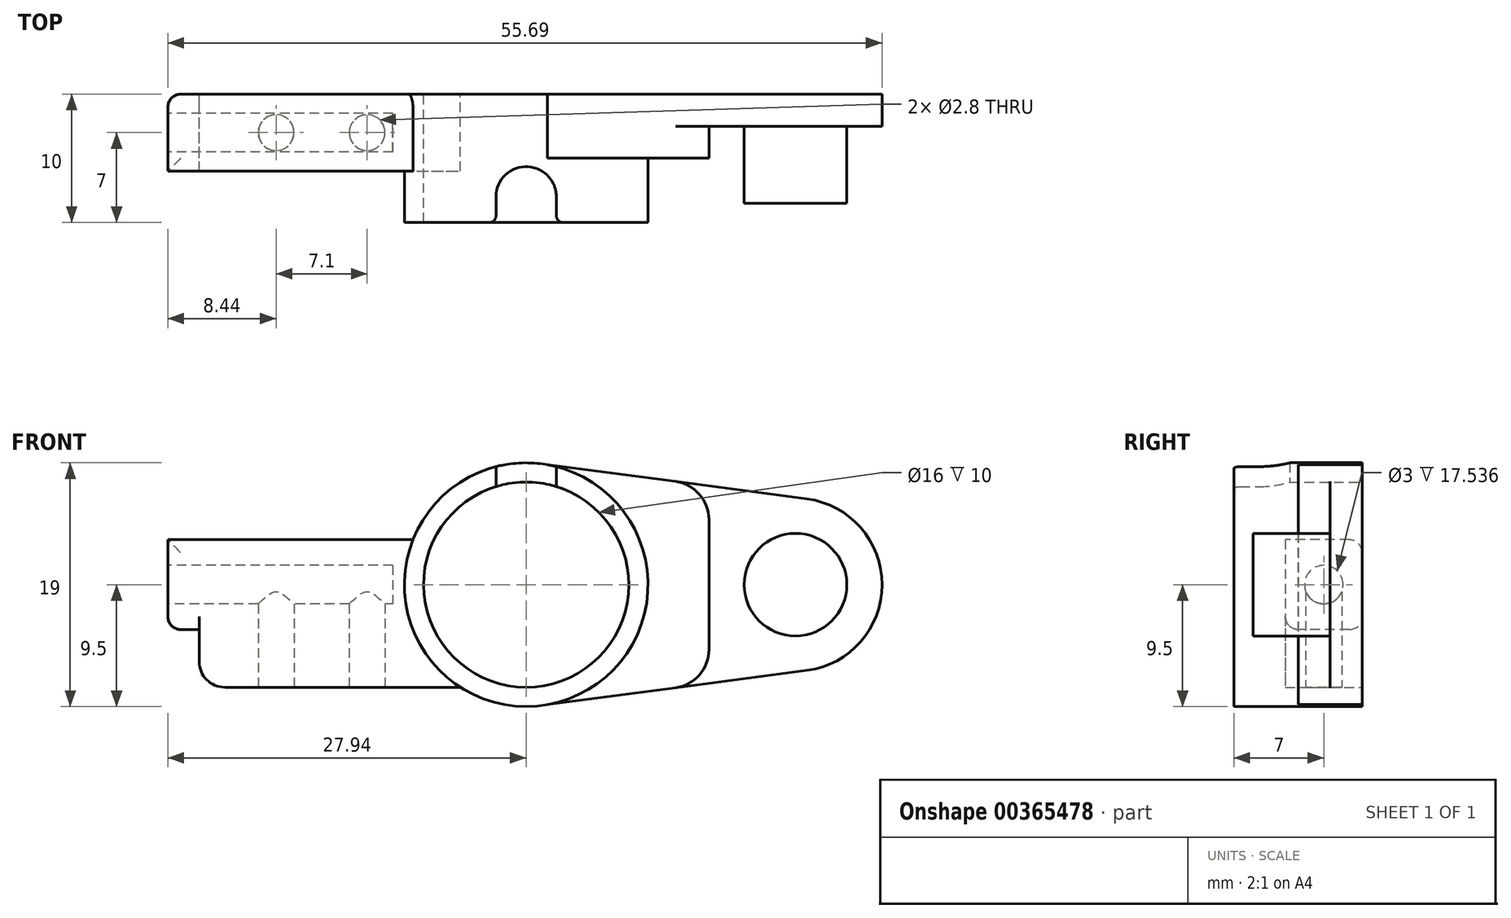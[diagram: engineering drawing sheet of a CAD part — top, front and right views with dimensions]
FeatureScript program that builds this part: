
annotation { "Feature Type Name" : "Feature", "Feature Type Description" : "" }
export const myFeature = defineFeature(function(context is Context, id is Id, definition is map)
    precondition{}
    {
        {
            var Q0;
            Q0=qCreatedBy(makeId("Front.planeOp"),FACE);
            var sketch = newSketch(context, id + "F0", { "sketchPlane" : qUnion([Q0])});
            skCircle(sketch, "E0", {"center": v(0, 0) * mm, "radius": 8 * mm});
            skCircle(sketch, "E1", {"center": v(0, 0) * mm, "radius": 9.5 * mm});
            skLineSegment(sketch, "E2", {"start": v(0, 0) * mm, "end": v(0, -1.5) * mm});
            skLineSegment(sketch, "E3", {"start": v(0, 0) * mm, "end": v(0, 1.5) * mm});
            skLineSegment(sketch, "E4", {"start": v(-32.5, 0) * mm, "end": v(-32.5, 1.5) * mm});
            skLineSegment(sketch, "E5", {"start": v(-32.5, 0) * mm, "end": v(-32.5, -1.5) * mm});
            skLineSegment(sketch, "E6", {"start": v(-32.5, -1.5) * mm, "end": v(-32.5, -2.5) * mm});
            skLineSegment(sketch, "E7", {"start": v(-23.5, -8) * mm, "end": v(-5.12, -8) * mm});
            skLineSegment(sketch, "E8.MirrorCS", {"start": v(-32.5, 1.5) * mm, "end": v(-32.5, 3.5) * mm});
            skLineSegment(sketch, "E9", {"start": v(-25.5, 0) * mm, "end": v(-25.5, -6) * mm});
            skLineSegment(sketch, "E10", {"start": v(-32.5, 1.5) * mm, "end": v(-32.5, 2.5) * mm});
            skLineSegment(sketch, "E11", {"start": v(-32.5, -1.5) * mm, "end": v(-32.5, -3.5) * mm});
            skLineSegment(sketch, "E12", {"start": v(-31.5, -3.5) * mm, "end": v(-25.5, -3.5) * mm});
            skLineSegment(sketch, "E13", {"start": v(-31.5, 3.5) * mm, "end": v(-25.5, 3.5) * mm});
            skPoint(sketch, "E14.orphan", {"position": v(-32.5, 8) * mm});
            skPoint(sketch, "E15.orphan", {"position": v(-32.5, -8) * mm});
            skPoint(sketch, "E16.visualSharp", {"position": v(-25.5, 8) * mm});
            skPoint(sketch, "E17.visualSharp", {"position": v(-25.5, -8) * mm});
            skArc(sketch, "E17.filletArc", {"start": v(-25.5, -6) * mm, "mid": v(-24.91, -7.41) * mm, "end": v(-23.5, -8) * mm});
            skPoint(sketch, "E18.visualSharp", {"position": v(-32.5, 3.5) * mm});
            skArc(sketch, "E18.filletArc", {"start": v(-31.5, 3.5) * mm, "mid": v(-32.2, 3.2) * mm, "end": v(-32.5, 2.5) * mm});
            skPoint(sketch, "E19.visualSharp", {"position": v(-32.5, -3.5) * mm});
            skArc(sketch, "E19.filletArc", {"start": v(-32.5, -2.5) * mm, "mid": v(-32.2, -3.2) * mm, "end": v(-31.5, -3.5) * mm});
            skPoint(sketch, "E20.orphan", {"position": v(-2.5, 8) * mm});
            skPoint(sketch, "E21.orphan", {"position": v(-2.5, -8) * mm});
            skLineSegment(sketch, "E22", {"start": v(-25.5, 3.5) * mm, "end": v(-8.83, 3.5) * mm});
            skLineSegment(sketch, "E23", {"start": v(-25.5, -3.5) * mm, "end": v(-25.5, 3) * mm});
            skLineSegment(sketch, "E24", {"start": v(-23.5, 5) * mm, "end": v(-8.08, 5) * mm});
            skPoint(sketch, "E25.visualSharp", {"position": v(-25.5, 5) * mm});
            skArc(sketch, "E25.filletArc", {"start": v(-23.5, 5) * mm, "mid": v(-24.91, 4.41) * mm, "end": v(-25.5, 3) * mm});
            skSolve(sketch);
        }
        {
            var Q0;
            Q0=qSketchRegion(id+"F0",true);
            extrude(context, id + "F1", {"entities" : qUnion([Q0]), "depth" : 10 * mm});
        }
        {
            var Q0;
            Q0=makeQuery(id+"F1.opExtrude","SWEPT_FACE",FACE,{"disambiguationData":[OSD([sQuery(id+"F0.wireOp",EDGE,"E7")])]});
            var sketch = newSketch(context, id + "F2", { "sketchPlane" : qUnion([Q0])});
            skLineSegment(sketch, "E26", {"start": v(-11, 3) * mm, "end": v(-12.4, 3) * mm});
            skCircle(sketch, "E27", {"center": v(-12.4, 3) * mm, "radius": 1.4 * mm});
            skLineSegment(sketch, "E28", {"start": v(-23.5, 5) * mm, "end": v(-22.5, 5) * mm});
            skCircle(sketch, "E29", {"center": v(-19.5, 3) * mm, "radius": 1.4 * mm});
            skSolve(sketch);
        }
        {
            var Q0;
            Q0=qSketchRegion(id+"F2",true);
            extrude(context, id + "F3", {"entities" : qUnion([Q0]), "operationType" : NewBodyOperationType.REMOVE, "oppositeDirection" : true, "depth" : 8 * mm});
        }
        {
            var Q0;
            Q0=qCreatedBy(makeId("Front.planeOp"),FACE);
            var sketch = newSketch(context, id + "F4", { "sketchPlane" : qUnion([Q0])});
            skLineSegment(sketch, "E30", {"start": v(8.71, 0) * mm, "end": v(21, 0) * mm});
            skCircle(sketch, "E31", {"center": v(21, 0) * mm, "radius": 6.75 * mm});
            skLineSegment(sketch, "E32", {"start": v(21, 0) * mm, "end": v(21, -5.45) * mm});
            skLineSegment(sketch, "E33", {"start": v(21, 0) * mm, "end": v(21.88, -6.7) * mm});
            skLineSegment(sketch, "E34", {"start": v(21.88, -6.7) * mm, "end": v(0.83, -9.46) * mm});
            skArc(sketch, "E35", {"start": v(0.83, -9.46) * mm, "mid": v(1.24, -9.42) * mm, "end": v(1.65, -9.36) * mm});
            skArc(sketch, "E36.MirrorCS", {"start": v(0.83, 9.46) * mm, "mid": v(1.24, 9.42) * mm, "end": v(1.65, 9.36) * mm});
            skLineSegment(sketch, "E37.MirrorCS", {"start": v(21.88, 6.7) * mm, "end": v(0.83, 9.46) * mm});
            skArc(sketch, "E38", {"start": v(0.83, -8.67) * mm, "mid": v(8.71, 0) * mm, "end": v(0.83, 8.67) * mm});
            skLineSegment(sketch, "E39", {"start": v(0.83, 9.46) * mm, "end": v(0.83, 8.67) * mm});
            skPoint(sketch, "E40.orphan", {"position": v(9.5, 0) * mm});
            skLineSegment(sketch, "E41.trimOffspring", {"start": v(0.83, -8.67) * mm, "end": v(0.83, -9.46) * mm});
            skSolve(sketch);
        }
        {
            var Q0;
            Q0=qSketchRegion(id+"F4",true);
            extrude(context, id + "F5", {"entities" : qUnion([Q0]), "operationType" : NewBodyOperationType.ADD, "depth" : 2.5 * mm});
        }
        {
            var Q0;
            Q0=makeQuery(id+"F5.opExtrude","CAP_FACE",FACE,{"disambiguationData":[OSD([sQuery(id+"F4.wireOp",EDGE,"E31"),sQuery(id+"F4.wireOp",EDGE,"E34"),sQuery(id+"F4.wireOp",EDGE,"E35"),sQuery(id+"F4.wireOp",EDGE,"E36.MirrorCS"),sQuery(id+"F4.wireOp",EDGE,"E37.MirrorCS"),sQuery(id+"F4.wireOp",EDGE,"E38"),sQuery(id+"F4.wireOp",EDGE,"E39"),sQuery(id+"F4.wireOp",EDGE,"E41.trimOffspring")])],"isStart":false});
            var sketch = newSketch(context, id + "F6", { "sketchPlane" : qUnion([Q0])});
            skCircle(sketch, "E42", {"center": v(21, 0) * mm, "radius": 4 * mm});
            skSolve(sketch);
        }
        {
            var Q0;
            Q0=qSketchRegion(id+"F6",true);
            extrude(context, id + "F7", {"entities" : qUnion([Q0]), "operationType" : NewBodyOperationType.ADD, "depth" : 6 * mm});
        }
        {
            var Q0;
            Q0=makeQuery(id+"F5.opExtrude","CAP_FACE",FACE,{"disambiguationData":[OSD([sQuery(id+"F4.wireOp",EDGE,"E31"),sQuery(id+"F4.wireOp",EDGE,"E34"),sQuery(id+"F4.wireOp",EDGE,"E35"),sQuery(id+"F4.wireOp",EDGE,"E36.MirrorCS"),sQuery(id+"F4.wireOp",EDGE,"E37.MirrorCS"),sQuery(id+"F4.wireOp",EDGE,"E38"),sQuery(id+"F4.wireOp",EDGE,"E39"),sQuery(id+"F4.wireOp",EDGE,"E41.trimOffspring")])],"isStart":false});
            var sketch = newSketch(context, id + "F8", { "sketchPlane" : qUnion([Q0])});
            skLineSegment(sketch, "E43", {"start": v(14.25, 0) * mm, "end": v(14.25, 7.7) * mm});
            skLineSegment(sketch, "E44", {"start": v(1.65, 9.36) * mm, "end": v(14.25, 7.7) * mm});
            skArc(sketch, "E45", {"start": v(1.65, -8.34) * mm, "mid": v(8.5, 0) * mm, "end": v(1.65, 8.34) * mm});
            skLineSegment(sketch, "E46", {"start": v(1.65, 9.36) * mm, "end": v(1.65, 8.34) * mm});
            skLineSegment(sketch, "E47.MirrorCS", {"start": v(1.65, -9.36) * mm, "end": v(1.65, -8.34) * mm});
            skLineSegment(sketch, "E48.MirrorCS", {"start": v(1.65, -9.36) * mm, "end": v(14.25, -7.7) * mm});
            skLineSegment(sketch, "E49.MirrorCS", {"start": v(14.25, 0) * mm, "end": v(14.25, -7.7) * mm});
            skPoint(sketch, "E50.start.orphan", {"position": v(9.5, 0) * mm});
            skSolve(sketch);
        }
        {
            var Q0;
            Q0=qSketchRegion(id+"F8",true);
            extrude(context, id + "F9", {"entities" : qUnion([Q0]), "operationType" : NewBodyOperationType.ADD, "depth" : 2.5 * mm});
        }
        {
            var Q0;
            Q0=makeQuery(id+"F9.opExtrude","SWEPT_EDGE",EDGE,{"disambiguationData":[OSD([sQuery(id+"F4.wireOp",EDGE,"E37.MirrorCS"),sQuery(id+"F8.wireOp",EDGE,"E43"),sQuery(id+"F8.wireOp",EDGE,"E44")])]});
            var Q1;
            Q1=makeQuery(id+"F9.opExtrude","SWEPT_EDGE",EDGE,{"disambiguationData":[OSD([sQuery(id+"F4.wireOp",EDGE,"E34"),sQuery(id+"F8.wireOp",EDGE,"E48.MirrorCS"),sQuery(id+"F8.wireOp",EDGE,"E49.MirrorCS")])]});
            fillet(context, id + "F10", {"entities" : qUnion([Q0, Q1]), "radius" : 3 * mm, "tangentPropagation" : true, "allowEdgeOverflow" : false});
        }
        {
            var Q0;
            Q0=qCreatedBy(makeId("Top.planeOp"),FACE);
            var sketch = newSketch(context, id + "F11", { "sketchPlane" : qUnion([Q0])});
            skLineSegment(sketch, "E51", {"start": v(0, 0) * mm, "end": v(0, -8) * mm});
            skCircle(sketch, "E52", {"center": v(0, -8) * mm, "radius": 2.35 * mm});
            skLineSegment(sketch, "E53.bottom", {"start": v(-2.35, -8) * mm, "end": v(2.35, -8) * mm});
            skLineSegment(sketch, "E53.top", {"start": v(-2.35, -11.86) * mm, "end": v(2.35, -11.86) * mm});
            skLineSegment(sketch, "E53.left", {"start": v(-2.35, -8) * mm, "end": v(-2.35, -11.86) * mm});
            skLineSegment(sketch, "E53.right", {"start": v(2.35, -8) * mm, "end": v(2.35, -11.86) * mm});
            skSolve(sketch);
        }
        {
            var Q0;
            Q0=qSketchRegion(id+"F11",true);
            extrude(context, id + "F12", {"entities" : qUnion([Q0]), "operationType" : NewBodyOperationType.REMOVE, "depth" : 25 * mm});
        }
        {
            var Q0;
            Q0=makeQuery(id+"F12.boolean.opBoolean","INTERSECT",EDGE,{"derivedFrom":[makeQuery(id+"F1.opExtrude","CAP_FACE",FACE,{"disambiguationData":[OSD([sQuery(id+"F0.wireOp",EDGE,"E0"),sQuery(id+"F0.wireOp",EDGE,"E1"),sQuery(id+"F0.wireOp",EDGE,"E4"),sQuery(id+"F0.wireOp",EDGE,"E5"),sQuery(id+"F0.wireOp",EDGE,"E7"),sQuery(id+"F0.wireOp",EDGE,"E9"),sQuery(id+"F0.wireOp",EDGE,"E10"),sQuery(id+"F0.wireOp",EDGE,"E11"),sQuery(id+"F0.wireOp",EDGE,"E12"),sQuery(id+"F0.wireOp",EDGE,"E13"),sQuery(id+"F0.wireOp",EDGE,"E17.filletArc"),sQuery(id+"F0.wireOp",EDGE,"E18.filletArc"),sQuery(id+"F0.wireOp",EDGE,"E19.filletArc"),sQuery(id+"F0.wireOp",EDGE,"E22"),sQuery(id+"F0.wireOp",EDGE,"E24"),sQuery(id+"F0.wireOp",EDGE,"E25.filletArc")])],"isStart":false}),makeQuery(id+"F12.opExtrude","SWEPT_FACE",FACE,{"disambiguationData":[OSD([sQuery(id+"F11.wireOp",EDGE,"E53.left")])]})]});
            var Q1;
            Q1=makeQuery(id+"F12.boolean.opBoolean","INTERSECT",EDGE,{"derivedFrom":[makeQuery(id+"F1.opExtrude","CAP_FACE",FACE,{"disambiguationData":[OSD([sQuery(id+"F0.wireOp",EDGE,"E0"),sQuery(id+"F0.wireOp",EDGE,"E1"),sQuery(id+"F0.wireOp",EDGE,"E4"),sQuery(id+"F0.wireOp",EDGE,"E5"),sQuery(id+"F0.wireOp",EDGE,"E7"),sQuery(id+"F0.wireOp",EDGE,"E9"),sQuery(id+"F0.wireOp",EDGE,"E10"),sQuery(id+"F0.wireOp",EDGE,"E11"),sQuery(id+"F0.wireOp",EDGE,"E12"),sQuery(id+"F0.wireOp",EDGE,"E13"),sQuery(id+"F0.wireOp",EDGE,"E17.filletArc"),sQuery(id+"F0.wireOp",EDGE,"E18.filletArc"),sQuery(id+"F0.wireOp",EDGE,"E19.filletArc"),sQuery(id+"F0.wireOp",EDGE,"E22"),sQuery(id+"F0.wireOp",EDGE,"E24"),sQuery(id+"F0.wireOp",EDGE,"E25.filletArc")])],"isStart":false}),makeQuery(id+"F12.opExtrude","SWEPT_FACE",FACE,{"disambiguationData":[OSD([sQuery(id+"F11.wireOp",EDGE,"E53.right")])]})]});
            fillet(context, id + "F13", {"entities" : qUnion([Q0, Q1]), "radius" : 0.5 * mm, "tangentPropagation" : true, "allowEdgeOverflow" : false});
        }
        {
            var Q0;
            Q0=makeQuery(id+"F1.opExtrude","CAP_FACE",FACE,{"disambiguationData":[OSD([sQuery(id+"F0.wireOp",EDGE,"E0"),sQuery(id+"F0.wireOp",EDGE,"E1"),sQuery(id+"F0.wireOp",EDGE,"E4"),sQuery(id+"F0.wireOp",EDGE,"E5"),sQuery(id+"F0.wireOp",EDGE,"E7"),sQuery(id+"F0.wireOp",EDGE,"E9"),sQuery(id+"F0.wireOp",EDGE,"E10"),sQuery(id+"F0.wireOp",EDGE,"E11"),sQuery(id+"F0.wireOp",EDGE,"E12"),sQuery(id+"F0.wireOp",EDGE,"E13"),sQuery(id+"F0.wireOp",EDGE,"E17.filletArc"),sQuery(id+"F0.wireOp",EDGE,"E18.filletArc"),sQuery(id+"F0.wireOp",EDGE,"E19.filletArc"),sQuery(id+"F0.wireOp",EDGE,"E22"),sQuery(id+"F0.wireOp",EDGE,"E24"),sQuery(id+"F0.wireOp",EDGE,"E25.filletArc")])],"isStart":false});
            var sketch = newSketch(context, id + "F14", { "sketchPlane" : qUnion([Q0])});
            skSolve(sketch);
        }
        {
            var Q0;
            Q0=makeQuery(id+"F1.opExtrude","SWEPT_FACE",FACE,{"disambiguationData":[OSD([sQuery(id+"F0.wireOp",EDGE,"E4"),sQuery(id+"F0.wireOp",EDGE,"E5"),sQuery(id+"F0.wireOp",EDGE,"E10"),sQuery(id+"F0.wireOp",EDGE,"E11")])]});
            var sketch = newSketch(context, id + "F15", { "sketchPlane" : qUnion([Q0])});
            skLineSegment(sketch, "E54", {"start": v(0, 0) * mm, "end": v(3, 0) * mm});
            skCircle(sketch, "E55", {"center": v(3, 0) * mm, "radius": 1.5 * mm});
            skLineSegment(sketch, "E56", {"start": v(3, 0) * mm, "end": v(6, 0) * mm});
            skSolve(sketch);
        }
        {
            var Q0;
            Q0 = qSketchRegion(id + "F15", true);
            extrude(context, id + "F16", {"entities" : qUnion([Q0]), "operationType" : NewBodyOperationType.REMOVE, "oppositeDirection" : true, "depth" : 22.1 * mm});
        }
        {
            var Q0;
            {var subQ11=sQuery(id+"F0.wireOp",EDGE,"E7");Q0=makeQuery(id+"F14.imprint","IMPRINT",FACE,{"disambiguationData":[TD([[makeQuery(id+"F14.imprint","IMPRINT",EDGE,{"derivedFrom":makeQuery(id+"F1.opExtrude","CAP_EDGE",EDGE,{"disambiguationData":[OSD([subQ11])],"isStart":false})}),1.0]])]});}
            var sketch = newSketch(context, id + "F17", { "sketchPlane" : qUnion([Q0])});
            skArc(sketch, "E57", {"start": v(-6.07, 7.3) * mm, "mid": v(-9.46, -0.82) * mm, "end": v(-4.73, -8.24) * mm});
            skLineSegment(sketch, "E58.bottom", {"start": v(-34.83, 7.3) * mm, "end": v(-6.07, 7.3) * mm});
            skLineSegment(sketch, "E58.top", {"start": v(-34.83, -9.59) * mm, "end": v(-4.73, -9.59) * mm});
            skLineSegment(sketch, "E58.left", {"start": v(-34.83, 7.3) * mm, "end": v(-34.83, -9.59) * mm});
            skLineSegment(sketch, "E58.right", {"start": v(-4.73, -8.24) * mm, "end": v(-4.73, -9.59) * mm});
            skSolve(sketch);
        }
        {
            var Q0;
            Q0 = qSketchRegion(id + "F17", true);
            extrude(context, id + "F18", {"entities" : qUnion([Q0]), "operationType" : NewBodyOperationType.REMOVE, "oppositeDirection" : true, "depth" : 4 * mm});
        }
        {
            var Q0;
            Q0=makeQuery(id+"F18.boolean.opBoolean","COPY",FACE,{"derivedFrom":makeQuery(id+"F18.opExtrude","CAP_FACE",FACE,{"disambiguationData":[OSD([sQuery(id+"F17.wireOp",EDGE,"E57"),sQuery(id+"F17.wireOp",EDGE,"E58.bottom"),sQuery(id+"F17.wireOp",EDGE,"E58.top"),sQuery(id+"F17.wireOp",EDGE,"E58.left"),sQuery(id+"F17.wireOp",EDGE,"E58.right")])],"isStart":false})});
            var sketch = newSketch(context, id + "F19", { "sketchPlane" : qUnion([Q0])});
            skArc(sketch, "E59", {"start": v(-7.5, 5.84) * mm, "mid": v(-8.25, 4.72) * mm, "end": v(-8.83, 3.5) * mm});
            skLineSegment(sketch, "E60.bottom", {"start": v(-25.44, 3.5) * mm, "end": v(-8.83, 3.5) * mm});
            skLineSegment(sketch, "E60.top", {"start": v(-25.44, 6.51) * mm, "end": v(-7.5, 6.51) * mm});
            skLineSegment(sketch, "E60.right", {"start": v(-7.5, 5.84) * mm, "end": v(-7.5, 6.51) * mm});
            skLineSegment(sketch, "E61", {"start": v(-25.44, 3.5) * mm, "end": v(-27.94, 3.5) * mm});
            skLineSegment(sketch, "E62", {"start": v(-27.94, 3.5) * mm, "end": v(-27.94, -7.75) * mm});
            skLineSegment(sketch, "E63", {"start": v(-27.94, -7.75) * mm, "end": v(-39, -7.75) * mm});
            skLineSegment(sketch, "E64", {"start": v(-39, -7.75) * mm, "end": v(-39, 6.51) * mm});
            skLineSegment(sketch, "E65", {"start": v(-39, 6.51) * mm, "end": v(-25.44, 6.51) * mm});
            skSolve(sketch);
        }
        {
            var Q0;
            Q0 = qSketchRegion(id + "F19", true);
            extrude(context, id + "F20", {"entities" : qUnion([Q0]), "operationType" : NewBodyOperationType.REMOVE, "oppositeDirection" : true, "depth" : 25 * mm});
        }
        {
            var Q0;
            Q0=makeQuery(id+"F20.boolean.opBoolean","COPY",EDGE,{"derivedFrom":makeQuery(id+"F20.opExtrude","SWEPT_EDGE",EDGE,{"disambiguationData":[OSD([sQuery(id+"F0.wireOp",EDGE,"E13"),sQuery(id+"F0.wireOp",EDGE,"E22"),sQuery(id+"F17.wireOp",EDGE,"E57"),sQuery(id+"F17.wireOp",EDGE,"E58.bottom"),sQuery(id+"F17.wireOp",EDGE,"E58.top"),sQuery(id+"F17.wireOp",EDGE,"E58.left"),sQuery(id+"F17.wireOp",EDGE,"E58.right"),sQuery(id+"F19.wireOp",EDGE,"E61"),sQuery(id+"F19.wireOp",EDGE,"E62")])]})});
            var Q1;
            Q1=makeQuery(id+"F20.boolean.opBoolean","INTERSECT",EDGE,{"derivedFrom":[makeQuery(id+"F1.opExtrude","SWEPT_FACE",FACE,{"disambiguationData":[OSD([sQuery(id+"F0.wireOp",EDGE,"E12")])]}),makeQuery(id+"F20.opExtrude","SWEPT_FACE",FACE,{"disambiguationData":[OSD([sQuery(id+"F19.wireOp",EDGE,"E62")])]})]});
            var Q2;
            Q2=makeQuery(id+"F20.boolean.opBoolean","COPY",EDGE,{"derivedFrom":makeQuery(id+"F20.opExtrude","CAP_EDGE",EDGE,{"disambiguationData":[OSD([sQuery(id+"F19.wireOp",EDGE,"E62")])],"isStart":true})});
            var Q3;
            Q3=makeQuery(id+"F20.boolean.opBoolean","INTERSECT",EDGE,{"derivedFrom":[makeQuery(id+"F5.boolean.opBoolean","MERGE",FACE,{"derivedFrom":[makeQuery(id+"F1.opExtrude","CAP_FACE",FACE,{"disambiguationData":[OSD([sQuery(id+"F0.wireOp",EDGE,"E0"),sQuery(id+"F0.wireOp",EDGE,"E1"),sQuery(id+"F0.wireOp",EDGE,"E4"),sQuery(id+"F0.wireOp",EDGE,"E5"),sQuery(id+"F0.wireOp",EDGE,"E7"),sQuery(id+"F0.wireOp",EDGE,"E9"),sQuery(id+"F0.wireOp",EDGE,"E10"),sQuery(id+"F0.wireOp",EDGE,"E11"),sQuery(id+"F0.wireOp",EDGE,"E12"),sQuery(id+"F0.wireOp",EDGE,"E13"),sQuery(id+"F0.wireOp",EDGE,"E17.filletArc"),sQuery(id+"F0.wireOp",EDGE,"E18.filletArc"),sQuery(id+"F0.wireOp",EDGE,"E19.filletArc"),sQuery(id+"F0.wireOp",EDGE,"E22"),sQuery(id+"F0.wireOp",EDGE,"E24"),sQuery(id+"F0.wireOp",EDGE,"E25.filletArc")])],"isStart":true}),makeQuery(id+"F5.opExtrude","CAP_FACE",FACE,{"disambiguationData":[OSD([sQuery(id+"F4.wireOp",EDGE,"E31"),sQuery(id+"F4.wireOp",EDGE,"E34"),sQuery(id+"F4.wireOp",EDGE,"E35"),sQuery(id+"F4.wireOp",EDGE,"E36.MirrorCS"),sQuery(id+"F4.wireOp",EDGE,"E37.MirrorCS"),sQuery(id+"F4.wireOp",EDGE,"E38"),sQuery(id+"F4.wireOp",EDGE,"E39"),sQuery(id+"F4.wireOp",EDGE,"E41.trimOffspring")])],"isStart":true})]}),makeQuery(id+"F20.opExtrude","SWEPT_FACE",FACE,{"disambiguationData":[OSD([sQuery(id+"F19.wireOp",EDGE,"E62")])]})]});
            var Q4;
            Q4=makeQuery(id+"F20.boolean.opBoolean","MERGE",EDGE,{"derivedFrom":[makeQuery(id+"F18.boolean.opBoolean","INTERSECT",EDGE,{"derivedFrom":[makeQuery(id+"F1.opExtrude","SWEPT_FACE",FACE,{"disambiguationData":[OSD([sQuery(id+"F0.wireOp",EDGE,"E13"),sQuery(id+"F0.wireOp",EDGE,"E22")])]}),makeQuery(id+"F18.opExtrude","CAP_FACE",FACE,{"disambiguationData":[OSD([sQuery(id+"F17.wireOp",EDGE,"E57"),sQuery(id+"F17.wireOp",EDGE,"E58.bottom"),sQuery(id+"F17.wireOp",EDGE,"E58.top"),sQuery(id+"F17.wireOp",EDGE,"E58.left"),sQuery(id+"F17.wireOp",EDGE,"E58.right")])],"isStart":false})]}),makeQuery(id+"F20.opExtrude","CAP_EDGE",EDGE,{"disambiguationData":[OSD([sQuery(id+"F19.wireOp",EDGE,"E60.bottom"),sQuery(id+"F19.wireOp",EDGE,"E61")])],"isStart":true})]});
            var Q5;
            Q5=makeQuery(id+"F20.boolean.opBoolean","INTERSECT",EDGE,{"derivedFrom":[makeQuery(id+"F5.boolean.opBoolean","MERGE",FACE,{"derivedFrom":[makeQuery(id+"F1.opExtrude","CAP_FACE",FACE,{"disambiguationData":[OSD([sQuery(id+"F0.wireOp",EDGE,"E0"),sQuery(id+"F0.wireOp",EDGE,"E1"),sQuery(id+"F0.wireOp",EDGE,"E4"),sQuery(id+"F0.wireOp",EDGE,"E5"),sQuery(id+"F0.wireOp",EDGE,"E7"),sQuery(id+"F0.wireOp",EDGE,"E9"),sQuery(id+"F0.wireOp",EDGE,"E10"),sQuery(id+"F0.wireOp",EDGE,"E11"),sQuery(id+"F0.wireOp",EDGE,"E12"),sQuery(id+"F0.wireOp",EDGE,"E13"),sQuery(id+"F0.wireOp",EDGE,"E17.filletArc"),sQuery(id+"F0.wireOp",EDGE,"E18.filletArc"),sQuery(id+"F0.wireOp",EDGE,"E19.filletArc"),sQuery(id+"F0.wireOp",EDGE,"E22"),sQuery(id+"F0.wireOp",EDGE,"E24"),sQuery(id+"F0.wireOp",EDGE,"E25.filletArc")])],"isStart":true}),makeQuery(id+"F5.opExtrude","CAP_FACE",FACE,{"disambiguationData":[OSD([sQuery(id+"F4.wireOp",EDGE,"E31"),sQuery(id+"F4.wireOp",EDGE,"E34"),sQuery(id+"F4.wireOp",EDGE,"E35"),sQuery(id+"F4.wireOp",EDGE,"E36.MirrorCS"),sQuery(id+"F4.wireOp",EDGE,"E37.MirrorCS"),sQuery(id+"F4.wireOp",EDGE,"E38"),sQuery(id+"F4.wireOp",EDGE,"E39"),sQuery(id+"F4.wireOp",EDGE,"E41.trimOffspring")])],"isStart":true})]}),makeQuery(id+"F20.opExtrude","SWEPT_FACE",FACE,{"disambiguationData":[OSD([sQuery(id+"F19.wireOp",EDGE,"E60.bottom"),sQuery(id+"F19.wireOp",EDGE,"E61")])]})]});
            var Q6;
            Q6=makeQuery(id+"F18.boolean.opBoolean","INTERSECT",EDGE,{"derivedFrom":[makeQuery(id+"F1.opExtrude","SWEPT_FACE",FACE,{"disambiguationData":[OSD([sQuery(id+"F0.wireOp",EDGE,"E12")])]}),makeQuery(id+"F18.opExtrude","CAP_FACE",FACE,{"disambiguationData":[OSD([sQuery(id+"F17.wireOp",EDGE,"E57"),sQuery(id+"F17.wireOp",EDGE,"E58.bottom"),sQuery(id+"F17.wireOp",EDGE,"E58.top"),sQuery(id+"F17.wireOp",EDGE,"E58.left"),sQuery(id+"F17.wireOp",EDGE,"E58.right")])],"isStart":false})]});
            var Q7;
            Q7=makeQuery(id+"F1.opExtrude","CAP_EDGE",EDGE,{"disambiguationData":[OSD([sQuery(id+"F0.wireOp",EDGE,"E12")])],"isStart":true});
            fillet(context, id + "F21", {"entities" : qUnion([Q0, Q1, Q2, Q3, Q4, Q5, Q6, Q7]), "radius" : 1 * mm, "tangentPropagation" : true, "allowEdgeOverflow" : false});
        }
    });
